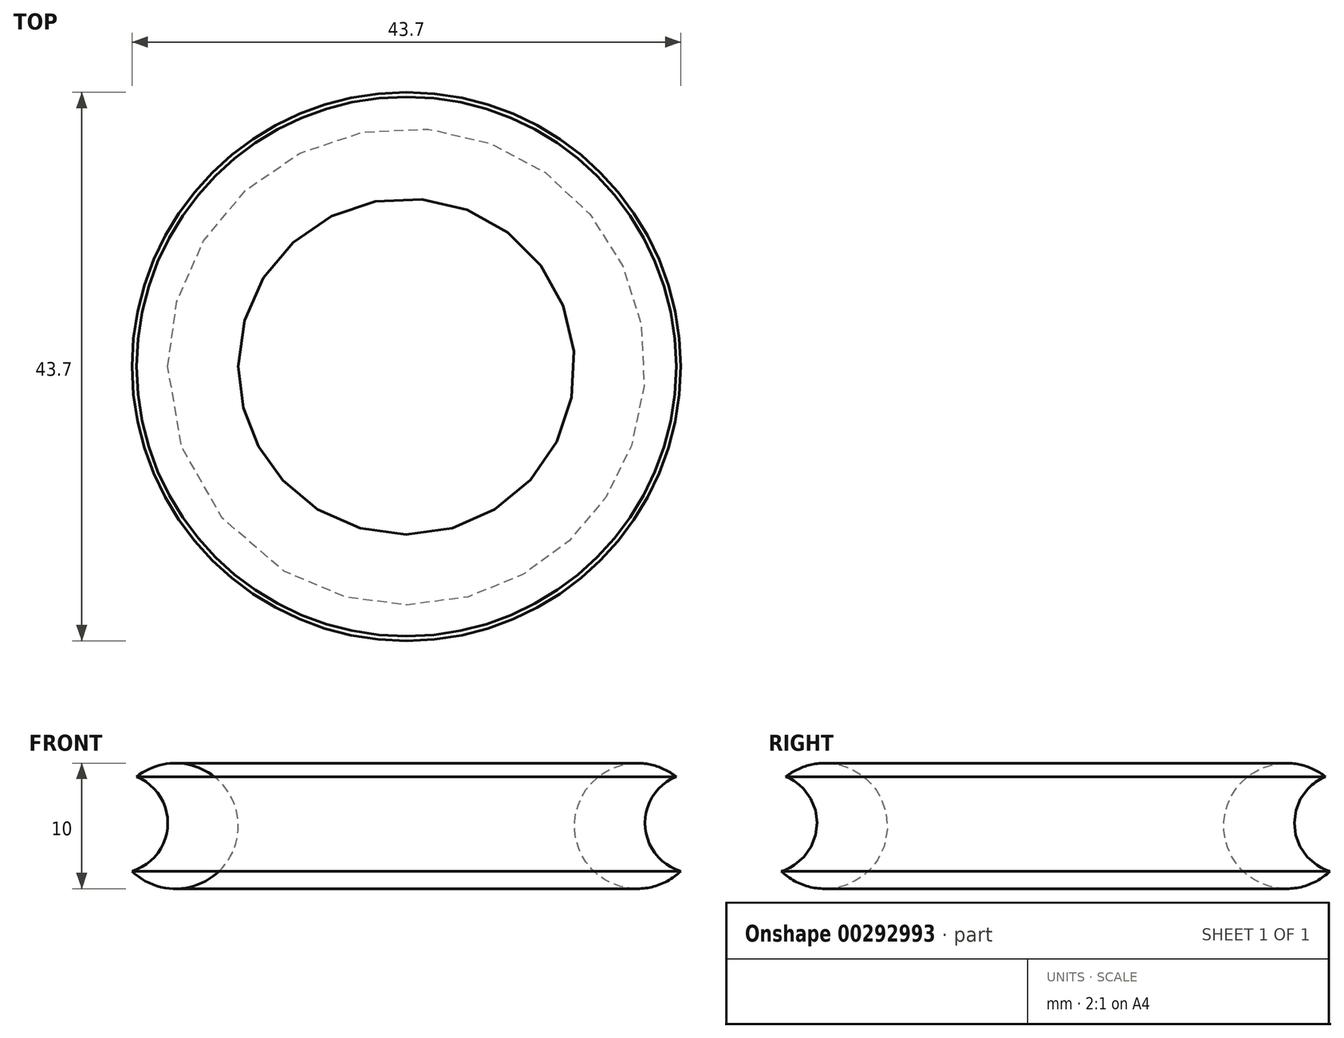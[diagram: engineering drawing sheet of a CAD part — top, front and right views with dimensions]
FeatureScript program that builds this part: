
annotation { "Feature Type Name" : "Feature", "Feature Type Description" : "" }
export const myFeature = defineFeature(function(context is Context, id is Id, definition is map)
    precondition{}
    {
        {
            var Q0;
            Q0=qCreatedBy(makeId("Right.planeOp"),FACE);
            var sketch = newSketch(context, id + "F0", { "sketchPlane" : qUnion([Q0])});
            skLineSegment(sketch, "E0", {"start": v(0, 0) * mm, "end": v(0, 127) * mm});
            skSolve(sketch);
        }
        {
            var Q0;
            Q0=qCreatedBy(makeId("Right.planeOp"),FACE);
            var sketch = newSketch(context, id + "F1", { "sketchPlane" : qUnion([Q0])});
            skCircle(sketch, "E1", {"center": v(18.39, 46.26) * mm, "radius": 5 * mm});
            skSolve(sketch);
        }
        {
            var Q0;
            Q0=makeQuery(id+"F1.imprint","IMPRINT",FACE,{"disambiguationData":[TD([[makeQuery(id+"F1.imprint","IMPRINT",EDGE,{"derivedFrom":sQuery(id+"F1.wireOp",EDGE,"E1")}),1.0]])]});
            var Q1;
            Q1=sQuery(id+"F0.wireOp",EDGE,"E0");
            revolve(context, id + "F2", {"entities" : qUnion([Q0]), "axis" : qUnion([Q1]), "revolveType" : RevolveType.FULL});
        }
        {
            var Q0;
            Q0=qCreatedBy(makeId("Front.planeOp"),FACE);
            var sketch = newSketch(context, id + "F3", { "sketchPlane" : qUnion([Q0])});
            skCircle(sketch, "E2", {"center": v(-23, 46.48) * mm, "radius": 4 * mm});
            skSolve(sketch);
        }
        {
            var Q0;
            Q0=makeQuery(id+"F3.imprint","IMPRINT",FACE,{"disambiguationData":[TD([[makeQuery(id+"F3.imprint","IMPRINT",EDGE,{"derivedFrom":sQuery(id+"F3.wireOp",EDGE,"E2")}),1.0]])]});
            var Q1;
            Q1=sQuery(id+"F0.wireOp",EDGE,"E0");
            revolve(context, id + "F4", {"operationType" : NewBodyOperationType.REMOVE, "entities" : qUnion([Q0]), "axis" : qUnion([Q1]), "revolveType" : RevolveType.FULL, "oppositeDirection" : true});
        }
    });
